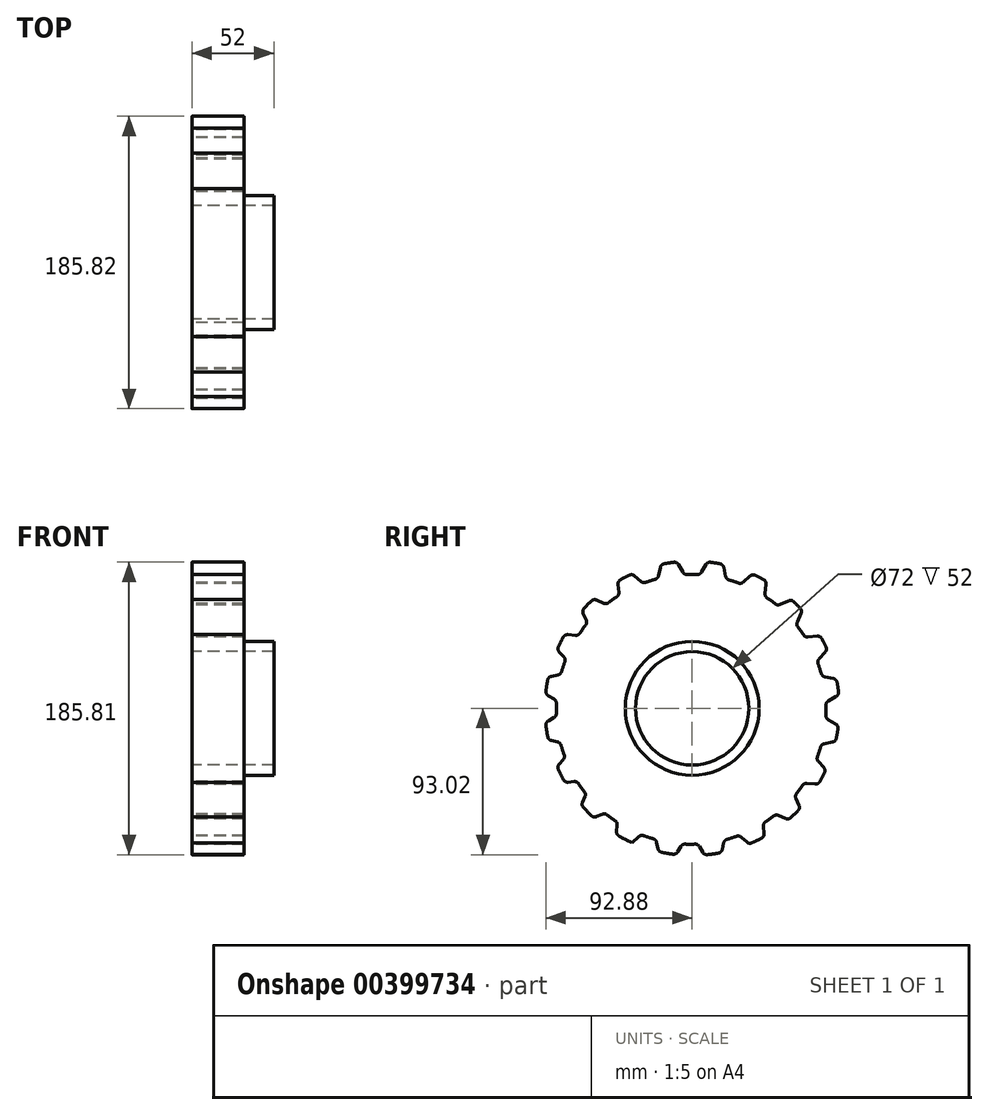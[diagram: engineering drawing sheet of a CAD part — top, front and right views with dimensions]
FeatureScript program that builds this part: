
annotation { "Feature Type Name" : "Feature", "Feature Type Description" : "" }
export const myFeature = defineFeature(function(context is Context, id is Id, definition is map)
    precondition{}
    {
        {
            var Q0;
            Q0=qCreatedBy(makeId("Right.planeOp"),FACE);
            var sketch = newSketch(context, id + "F0", { "sketchPlane" : qUnion([Q0])});
            skCircle(sketch, "E0", {"center": v(0, 0) * mm, "radius": 93.5 * mm});
            skCircle(sketch, "E1", {"center": v(0, 0) * mm, "radius": 42.5 * mm});
            skSolve(sketch);
        }
        {
            var Q0;
            Q0=makeQuery(id+"F0.imprint","IMPRINT",FACE,{"disambiguationData":[TD([[makeQuery(id+"F0.imprint","IMPRINT",EDGE,{"derivedFrom":sQuery(id+"F0.wireOp",EDGE,"E0")}),1.0]])]});
            extrude(context, id + "F1", {"entities" : qUnion([Q0]), "depth" : (347.5 + 33) * mm, "hasSecondDirection" : true, "secondDirectionOppositeDirection" : true, "secondDirectionDepth" : -347.5 * mm});
        }
        {
            var Q0;
            Q0=qCreatedBy(makeId("Right.planeOp"),FACE);
            var sketch = newSketch(context, id + "F2", { "sketchPlane" : qUnion([Q0])});
            skCircle(sketch, "E2", {"center": v(0, 0) * mm, "radius": 42.5 * mm});
            skCircle(sketch, "E3", {"center": v(0, 0) * mm, "radius": 36 * mm});
            skSolve(sketch);
        }
        {
            var Q0;
            Q0=makeQuery(id+"F2.imprint","IMPRINT",FACE,{"disambiguationData":[TD([[makeQuery(id+"F2.imprint","IMPRINT",EDGE,{"derivedFrom":sQuery(id+"F2.wireOp",EDGE,"E2")}),1.0]])]});
            extrude(context, id + "F3", {"entities" : qUnion([Q0]), "operationType" : NewBodyOperationType.ADD, "depth" : (347.5 + 52) * mm, "hasSecondDirection" : true, "secondDirectionOppositeDirection" : true, "secondDirectionDepth" : -347.5 * mm});
        }
        {
            var Q0;
            Q0=qCreatedBy(makeId("Right.planeOp"),FACE);
            var sketch = newSketch(context, id + "F4", { "sketchPlane" : qUnion([Q0])});
            skArc(sketch, "E4", {"start": v(3.2, 84.94) * mm, "mid": v(0, 85) * mm, "end": v(-3.2, 84.94) * mm});
            skCircle(sketch, "E5", {"center": v(180, 0) * mm, "radius": 95 * mm, "construction": true});
            skLineSegment(sketch, "E6", {"start": v(-5.91, 86.44) * mm, "end": v(-11.3, 95.76) * mm});
            skLineSegment(sketch, "E7", {"start": v(-11.3, 95.76) * mm, "end": v(11.3, 95.76) * mm});
            skLineSegment(sketch, "E8", {"start": v(11.3, 95.76) * mm, "end": v(5.91, 86.44) * mm});
            skLineSegment(sketch, "E9.1.0", {"start": v(-19.09, 94.74) * mm, "end": v(-21.7, 82.42) * mm});
            skArc(sketch, "E9.1.1", {"start": v(-21.7, 82.42) * mm, "mid": v(-26.5, 81.01) * mm, "end": v(-31.22, 79.33) * mm});
            skLineSegment(sketch, "E9.1.2", {"start": v(-40.58, 87.76) * mm, "end": v(-19.09, 94.74) * mm});
            skLineSegment(sketch, "E9.1.3", {"start": v(-31.22, 79.33) * mm, "end": v(-40.58, 87.76) * mm});
            skLineSegment(sketch, "E9.2.0", {"start": v(-47.67, 84.38) * mm, "end": v(-46.35, 71.85) * mm});
            skArc(sketch, "E9.2.1", {"start": v(-46.35, 71.85) * mm, "mid": v(-50.48, 69.03) * mm, "end": v(-54.44, 65.97) * mm});
            skLineSegment(sketch, "E9.2.2", {"start": v(-65.95, 71.1) * mm, "end": v(-47.67, 84.38) * mm});
            skLineSegment(sketch, "E9.2.3", {"start": v(-54.44, 65.97) * mm, "end": v(-65.95, 71.1) * mm});
            skLineSegment(sketch, "E9.3.0", {"start": v(-71.65, 65.7) * mm, "end": v(-66.52, 54.19) * mm});
            skArc(sketch, "E9.3.1", {"start": v(-66.52, 54.19) * mm, "mid": v(-69.58, 50.23) * mm, "end": v(-72.4, 46.1) * mm});
            skLineSegment(sketch, "E9.3.2", {"start": v(-84.93, 47.41) * mm, "end": v(-71.65, 65.7) * mm});
            skLineSegment(sketch, "E9.3.3", {"start": v(-72.4, 46.1) * mm, "end": v(-84.93, 47.41) * mm});
            skLineSegment(sketch, "E9.4.0", {"start": v(-88.68, 40.51) * mm, "end": v(-80.25, 31.15) * mm});
            skArc(sketch, "E9.4.1", {"start": v(-80.25, 31.15) * mm, "mid": v(-81.94, 26.44) * mm, "end": v(-83.34, 21.64) * mm});
            skLineSegment(sketch, "E9.4.2", {"start": v(-95.67, 19.02) * mm, "end": v(-88.68, 40.51) * mm});
            skLineSegment(sketch, "E9.4.3", {"start": v(-83.34, 21.64) * mm, "end": v(-95.67, 19.02) * mm});
            skLineSegment(sketch, "E9.5.0", {"start": v(-97.1, 11.3) * mm, "end": v(-86.19, 5) * mm});
            skArc(sketch, "E9.5.1", {"start": v(-86.19, 5) * mm, "mid": v(-86.34, 0) * mm, "end": v(-86.19, -5) * mm});
            skLineSegment(sketch, "E9.5.2", {"start": v(-97.1, -11.3) * mm, "end": v(-97.1, 11.3) * mm});
            skLineSegment(sketch, "E9.5.3", {"start": v(-86.19, -5) * mm, "end": v(-97.1, -11.3) * mm});
            skLineSegment(sketch, "E9.6.0", {"start": v(-96.08, -19.09) * mm, "end": v(-83.75, -21.7) * mm});
            skArc(sketch, "E9.6.1", {"start": v(-83.75, -21.7) * mm, "mid": v(-82.35, -26.5) * mm, "end": v(-80.66, -31.22) * mm});
            skLineSegment(sketch, "E9.6.2", {"start": v(-89.1, -40.58) * mm, "end": v(-96.08, -19.09) * mm});
            skLineSegment(sketch, "E9.6.3", {"start": v(-80.66, -31.22) * mm, "end": v(-89.1, -40.58) * mm});
            skLineSegment(sketch, "E9.7.0", {"start": v(-85.72, -47.67) * mm, "end": v(-73.19, -46.35) * mm});
            skArc(sketch, "E9.7.1", {"start": v(-73.19, -46.35) * mm, "mid": v(-70.37, -50.48) * mm, "end": v(-67.3, -54.44) * mm});
            skLineSegment(sketch, "E9.7.2", {"start": v(-72.43, -65.95) * mm, "end": v(-85.72, -47.67) * mm});
            skLineSegment(sketch, "E9.7.3", {"start": v(-67.3, -54.44) * mm, "end": v(-72.43, -65.95) * mm});
            skLineSegment(sketch, "E9.8.0", {"start": v(-67.03, -71.65) * mm, "end": v(-55.52, -66.52) * mm});
            skArc(sketch, "E9.8.1", {"start": v(-55.52, -66.52) * mm, "mid": v(-51.56, -69.58) * mm, "end": v(-47.43, -72.4) * mm});
            skLineSegment(sketch, "E9.8.2", {"start": v(-48.75, -84.93) * mm, "end": v(-67.03, -71.65) * mm});
            skLineSegment(sketch, "E9.8.3", {"start": v(-47.43, -72.4) * mm, "end": v(-48.75, -84.93) * mm});
            skLineSegment(sketch, "E9.9.0", {"start": v(-41.85, -88.68) * mm, "end": v(-32.49, -80.25) * mm});
            skArc(sketch, "E9.9.1", {"start": v(-32.49, -80.25) * mm, "mid": v(-27.78, -81.94) * mm, "end": v(-22.97, -83.34) * mm});
            skLineSegment(sketch, "E9.9.2", {"start": v(-20.36, -95.67) * mm, "end": v(-41.85, -88.68) * mm});
            skLineSegment(sketch, "E9.9.3", {"start": v(-22.97, -83.34) * mm, "end": v(-20.36, -95.67) * mm});
            skLineSegment(sketch, "E9.10.0", {"start": v(-12.64, -97.1) * mm, "end": v(-6.34, -86.19) * mm});
            skArc(sketch, "E9.10.1", {"start": v(-6.34, -86.19) * mm, "mid": v(-1.34, -86.34) * mm, "end": v(3.66, -86.19) * mm});
            skLineSegment(sketch, "E9.10.2", {"start": v(9.96, -97.1) * mm, "end": v(-12.64, -97.1) * mm});
            skLineSegment(sketch, "E9.10.3", {"start": v(3.66, -86.19) * mm, "end": v(9.96, -97.1) * mm});
            skLineSegment(sketch, "E9.11.0", {"start": v(17.75, -96.08) * mm, "end": v(20.37, -83.75) * mm});
            skArc(sketch, "E9.11.1", {"start": v(20.37, -83.75) * mm, "mid": v(25.17, -82.35) * mm, "end": v(29.88, -80.66) * mm});
            skLineSegment(sketch, "E9.11.2", {"start": v(39.24, -89.1) * mm, "end": v(17.75, -96.08) * mm});
            skLineSegment(sketch, "E9.11.3", {"start": v(29.88, -80.66) * mm, "end": v(39.24, -89.1) * mm});
            skLineSegment(sketch, "E9.12.0", {"start": v(46.33, -85.72) * mm, "end": v(45.01, -73.19) * mm});
            skArc(sketch, "E9.12.1", {"start": v(45.01, -73.19) * mm, "mid": v(49.15, -70.37) * mm, "end": v(53.1, -67.3) * mm});
            skLineSegment(sketch, "E9.12.2", {"start": v(64.62, -72.43) * mm, "end": v(46.33, -85.72) * mm});
            skLineSegment(sketch, "E9.12.3", {"start": v(53.1, -67.3) * mm, "end": v(64.62, -72.43) * mm});
            skLineSegment(sketch, "E9.13.0", {"start": v(70.31, -67.03) * mm, "end": v(65.19, -55.52) * mm});
            skArc(sketch, "E9.13.1", {"start": v(65.19, -55.52) * mm, "mid": v(68.25, -51.56) * mm, "end": v(71.07, -47.43) * mm});
            skLineSegment(sketch, "E9.13.2", {"start": v(83.6, -48.75) * mm, "end": v(70.31, -67.03) * mm});
            skLineSegment(sketch, "E9.13.3", {"start": v(71.07, -47.43) * mm, "end": v(83.6, -48.75) * mm});
            skLineSegment(sketch, "E9.14.0", {"start": v(87.35, -41.85) * mm, "end": v(78.92, -32.49) * mm});
            skArc(sketch, "E9.14.1", {"start": v(78.92, -32.49) * mm, "mid": v(80.6, -27.78) * mm, "end": v(82, -22.97) * mm});
            skLineSegment(sketch, "E9.14.2", {"start": v(94.33, -20.36) * mm, "end": v(87.35, -41.85) * mm});
            skLineSegment(sketch, "E9.14.3", {"start": v(82, -22.97) * mm, "end": v(94.33, -20.36) * mm});
            skLineSegment(sketch, "E9.15.0", {"start": v(95.76, -12.64) * mm, "end": v(84.85, -6.34) * mm});
            skArc(sketch, "E9.15.1", {"start": v(84.85, -6.34) * mm, "mid": v(85, -1.34) * mm, "end": v(84.85, 3.66) * mm});
            skLineSegment(sketch, "E9.15.2", {"start": v(95.76, 9.96) * mm, "end": v(95.76, -12.64) * mm});
            skLineSegment(sketch, "E9.15.3", {"start": v(84.85, 3.66) * mm, "end": v(95.76, 9.96) * mm});
            skLineSegment(sketch, "E9.16.0", {"start": v(94.74, 17.75) * mm, "end": v(82.42, 20.37) * mm});
            skArc(sketch, "E9.16.1", {"start": v(82.42, 20.37) * mm, "mid": v(81.01, 25.17) * mm, "end": v(79.33, 29.88) * mm});
            skLineSegment(sketch, "E9.16.2", {"start": v(87.76, 39.24) * mm, "end": v(94.74, 17.75) * mm});
            skLineSegment(sketch, "E9.16.3", {"start": v(79.33, 29.88) * mm, "end": v(87.76, 39.24) * mm});
            skLineSegment(sketch, "E9.17.0", {"start": v(84.38, 46.33) * mm, "end": v(71.85, 45.01) * mm});
            skArc(sketch, "E9.17.1", {"start": v(71.85, 45.01) * mm, "mid": v(69.03, 49.15) * mm, "end": v(65.97, 53.1) * mm});
            skLineSegment(sketch, "E9.17.2", {"start": v(71.1, 64.62) * mm, "end": v(84.38, 46.33) * mm});
            skLineSegment(sketch, "E9.17.3", {"start": v(65.97, 53.1) * mm, "end": v(71.1, 64.62) * mm});
            skLineSegment(sketch, "E9.18.0", {"start": v(65.7, 70.31) * mm, "end": v(54.19, 65.19) * mm});
            skArc(sketch, "E9.18.1", {"start": v(54.19, 65.19) * mm, "mid": v(50.23, 68.25) * mm, "end": v(46.1, 71.07) * mm});
            skLineSegment(sketch, "E9.18.2", {"start": v(47.41, 83.6) * mm, "end": v(65.7, 70.31) * mm});
            skLineSegment(sketch, "E9.18.3", {"start": v(46.1, 71.07) * mm, "end": v(47.41, 83.6) * mm});
            skLineSegment(sketch, "E9.19.0", {"start": v(40.51, 87.35) * mm, "end": v(31.15, 78.92) * mm});
            skArc(sketch, "E9.19.1", {"start": v(31.15, 78.92) * mm, "mid": v(26.44, 80.6) * mm, "end": v(21.64, 82) * mm});
            skLineSegment(sketch, "E9.19.2", {"start": v(19.02, 94.33) * mm, "end": v(40.51, 87.35) * mm});
            skLineSegment(sketch, "E9.19.3", {"start": v(21.64, 82) * mm, "end": v(19.02, 94.33) * mm});
            skPoint(sketch, "E9.center", {"position": v(-0.67, -0.67) * mm});
            skPoint(sketch, "E10.visualSharp", {"position": v(-5, 84.85) * mm});
            skArc(sketch, "E10.filletArc", {"start": v(-5.91, 86.44) * mm, "mid": v(-4.77, 85.31) * mm, "end": v(-3.2, 84.94) * mm});
            skPoint(sketch, "E11.visualSharp", {"position": v(5, 84.85) * mm});
            skArc(sketch, "E11.filletArc", {"start": v(3.2, 84.94) * mm, "mid": v(4.77, 85.31) * mm, "end": v(5.91, 86.44) * mm});
            skSolve(sketch);
        }
        {
            var Q0;
            Q0 = qSketchRegion(id + "F4", true);
            extrude(context, id + "F5", {"entities" : qUnion([Q0]), "depth" : 473 * mm});
        }
        {
            var Q0;
            Q0=makeQuery(id+"F5.opExtrude","SWEPT_BODY",BODY,{"disambiguationData":[OSD([sQuery(id+"F4.wireOp",EDGE,"E4"),sQuery(id+"F4.wireOp",EDGE,"E6"),sQuery(id+"F4.wireOp",EDGE,"E7"),sQuery(id+"F4.wireOp",EDGE,"E8")])]});
            var Q1;
            Q1=makeQuery(id+"F1.opExtrude","SWEPT_BODY",BODY,{"disambiguationData":[OSD([sQuery(id+"F0.wireOp",EDGE,"E0"),sQuery(id+"F0.wireOp",EDGE,"E1")])]});
            booleanBodies(context, id + "F6", {"operationType" : BooleanOperationType.SUBTRACTION, "tools" : qUnion([Q0]), "targets" : qUnion([Q1])});
        }
        {
            var Q0;
            Q0=makeQuery(id+"F5.opExtrude","SWEPT_BODY",BODY,{"disambiguationData":[OSD([sQuery(id+"F4.wireOp",EDGE,"E9.1.0"),sQuery(id+"F4.wireOp",EDGE,"E9.1.1"),sQuery(id+"F4.wireOp",EDGE,"E9.1.2"),sQuery(id+"F4.wireOp",EDGE,"E9.1.3")])]});
            var Q1;
            Q1=makeQuery(id+"F5.opExtrude","SWEPT_BODY",BODY,{"disambiguationData":[OSD([sQuery(id+"F4.wireOp",EDGE,"E9.2.0"),sQuery(id+"F4.wireOp",EDGE,"E9.2.1"),sQuery(id+"F4.wireOp",EDGE,"E9.2.2"),sQuery(id+"F4.wireOp",EDGE,"E9.2.3")])]});
            var Q2;
            Q2=makeQuery(id+"F5.opExtrude","SWEPT_BODY",BODY,{"disambiguationData":[OSD([sQuery(id+"F4.wireOp",EDGE,"E9.3.0"),sQuery(id+"F4.wireOp",EDGE,"E9.3.1"),sQuery(id+"F4.wireOp",EDGE,"E9.3.2"),sQuery(id+"F4.wireOp",EDGE,"E9.3.3")])]});
            var Q3;
            Q3=makeQuery(id+"F5.opExtrude","SWEPT_BODY",BODY,{"disambiguationData":[OSD([sQuery(id+"F4.wireOp",EDGE,"E9.4.0"),sQuery(id+"F4.wireOp",EDGE,"E9.4.1"),sQuery(id+"F4.wireOp",EDGE,"E9.4.2"),sQuery(id+"F4.wireOp",EDGE,"E9.4.3")])]});
            var Q4;
            Q4=makeQuery(id+"F5.opExtrude","SWEPT_BODY",BODY,{"disambiguationData":[OSD([sQuery(id+"F4.wireOp",EDGE,"E9.5.0"),sQuery(id+"F4.wireOp",EDGE,"E9.5.1"),sQuery(id+"F4.wireOp",EDGE,"E9.5.2"),sQuery(id+"F4.wireOp",EDGE,"E9.5.3")])]});
            var Q5;
            Q5=makeQuery(id+"F5.opExtrude","SWEPT_BODY",BODY,{"disambiguationData":[OSD([sQuery(id+"F4.wireOp",EDGE,"E9.6.0"),sQuery(id+"F4.wireOp",EDGE,"E9.6.1"),sQuery(id+"F4.wireOp",EDGE,"E9.6.2"),sQuery(id+"F4.wireOp",EDGE,"E9.6.3")])]});
            var Q6;
            Q6=makeQuery(id+"F5.opExtrude","SWEPT_BODY",BODY,{"disambiguationData":[OSD([sQuery(id+"F4.wireOp",EDGE,"E9.7.0"),sQuery(id+"F4.wireOp",EDGE,"E9.7.1"),sQuery(id+"F4.wireOp",EDGE,"E9.7.2"),sQuery(id+"F4.wireOp",EDGE,"E9.7.3")])]});
            var Q7;
            Q7=makeQuery(id+"F5.opExtrude","SWEPT_BODY",BODY,{"disambiguationData":[OSD([sQuery(id+"F4.wireOp",EDGE,"E9.8.0"),sQuery(id+"F4.wireOp",EDGE,"E9.8.1"),sQuery(id+"F4.wireOp",EDGE,"E9.8.2"),sQuery(id+"F4.wireOp",EDGE,"E9.8.3")])]});
            var Q8;
            Q8=makeQuery(id+"F5.opExtrude","SWEPT_BODY",BODY,{"disambiguationData":[OSD([sQuery(id+"F4.wireOp",EDGE,"E9.9.0"),sQuery(id+"F4.wireOp",EDGE,"E9.9.1"),sQuery(id+"F4.wireOp",EDGE,"E9.9.2"),sQuery(id+"F4.wireOp",EDGE,"E9.9.3")])]});
            var Q9;
            Q9=makeQuery(id+"F5.opExtrude","SWEPT_BODY",BODY,{"disambiguationData":[OSD([sQuery(id+"F4.wireOp",EDGE,"E9.10.0"),sQuery(id+"F4.wireOp",EDGE,"E9.10.1"),sQuery(id+"F4.wireOp",EDGE,"E9.10.2"),sQuery(id+"F4.wireOp",EDGE,"E9.10.3")])]});
            var Q10;
            Q10=makeQuery(id+"F5.opExtrude","SWEPT_BODY",BODY,{"disambiguationData":[OSD([sQuery(id+"F4.wireOp",EDGE,"E9.11.0"),sQuery(id+"F4.wireOp",EDGE,"E9.11.1"),sQuery(id+"F4.wireOp",EDGE,"E9.11.2"),sQuery(id+"F4.wireOp",EDGE,"E9.11.3")])]});
            var Q11;
            Q11=makeQuery(id+"F5.opExtrude","SWEPT_BODY",BODY,{"disambiguationData":[OSD([sQuery(id+"F4.wireOp",EDGE,"E9.12.0"),sQuery(id+"F4.wireOp",EDGE,"E9.12.1"),sQuery(id+"F4.wireOp",EDGE,"E9.12.2"),sQuery(id+"F4.wireOp",EDGE,"E9.12.3")])]});
            var Q12;
            Q12=makeQuery(id+"F5.opExtrude","SWEPT_BODY",BODY,{"disambiguationData":[OSD([sQuery(id+"F4.wireOp",EDGE,"E9.13.0"),sQuery(id+"F4.wireOp",EDGE,"E9.13.1"),sQuery(id+"F4.wireOp",EDGE,"E9.13.2"),sQuery(id+"F4.wireOp",EDGE,"E9.13.3")])]});
            var Q13;
            Q13=makeQuery(id+"F5.opExtrude","SWEPT_BODY",BODY,{"disambiguationData":[OSD([sQuery(id+"F4.wireOp",EDGE,"E9.14.0"),sQuery(id+"F4.wireOp",EDGE,"E9.14.1"),sQuery(id+"F4.wireOp",EDGE,"E9.14.2"),sQuery(id+"F4.wireOp",EDGE,"E9.14.3")])]});
            var Q14;
            Q14=makeQuery(id+"F5.opExtrude","SWEPT_BODY",BODY,{"disambiguationData":[OSD([sQuery(id+"F4.wireOp",EDGE,"E9.15.0"),sQuery(id+"F4.wireOp",EDGE,"E9.15.1"),sQuery(id+"F4.wireOp",EDGE,"E9.15.2"),sQuery(id+"F4.wireOp",EDGE,"E9.15.3")])]});
            var Q15;
            Q15=makeQuery(id+"F5.opExtrude","SWEPT_BODY",BODY,{"disambiguationData":[OSD([sQuery(id+"F4.wireOp",EDGE,"E9.16.0"),sQuery(id+"F4.wireOp",EDGE,"E9.16.1"),sQuery(id+"F4.wireOp",EDGE,"E9.16.2"),sQuery(id+"F4.wireOp",EDGE,"E9.16.3")])]});
            var Q16;
            Q16=makeQuery(id+"F5.opExtrude","SWEPT_BODY",BODY,{"disambiguationData":[OSD([sQuery(id+"F4.wireOp",EDGE,"E9.17.0"),sQuery(id+"F4.wireOp",EDGE,"E9.17.1"),sQuery(id+"F4.wireOp",EDGE,"E9.17.2"),sQuery(id+"F4.wireOp",EDGE,"E9.17.3")])]});
            var Q17;
            Q17=makeQuery(id+"F5.opExtrude","SWEPT_BODY",BODY,{"disambiguationData":[OSD([sQuery(id+"F4.wireOp",EDGE,"E9.18.0"),sQuery(id+"F4.wireOp",EDGE,"E9.18.1"),sQuery(id+"F4.wireOp",EDGE,"E9.18.2"),sQuery(id+"F4.wireOp",EDGE,"E9.18.3")])]});
            var Q18;
            Q18=makeQuery(id+"F5.opExtrude","SWEPT_BODY",BODY,{"disambiguationData":[OSD([sQuery(id+"F4.wireOp",EDGE,"E9.19.0"),sQuery(id+"F4.wireOp",EDGE,"E9.19.1"),sQuery(id+"F4.wireOp",EDGE,"E9.19.2"),sQuery(id+"F4.wireOp",EDGE,"E9.19.3")])]});
            var Q19;
            Q19=makeQuery(id+"F1.opExtrude","SWEPT_BODY",BODY,{"disambiguationData":[OSD([sQuery(id+"F0.wireOp",EDGE,"E0"),sQuery(id+"F0.wireOp",EDGE,"E1")])]});
            booleanBodies(context, id + "F7", {"operationType" : BooleanOperationType.SUBTRACTION, "tools" : qUnion([Q0, Q1, Q2, Q3, Q4, Q5, Q6, Q7, Q8, Q9, Q10, Q11, Q12, Q13, Q14, Q15, Q16, Q17, Q18]), "targets" : qUnion([Q19])});
        }
        {
            var Q0;
            Q0=makeQuery(id+"F6.opBoolean","INTERSECT",EDGE,{"derivedFrom":[makeQuery(id+"F1.opExtrude","SWEPT_FACE",FACE,{"disambiguationData":[OSD([sQuery(id+"F0.wireOp",EDGE,"E0")])]}),makeQuery(id+"F5.opExtrude","SWEPT_FACE",FACE,{"disambiguationData":[OSD([sQuery(id+"F4.wireOp",EDGE,"E6")])]})]});
            var Q1;
            Q1=makeQuery(id+"F7.opBoolean","INTERSECT",EDGE,{"derivedFrom":[makeQuery(id+"F5.opExtrude","SWEPT_FACE",FACE,{"disambiguationData":[OSD([sQuery(id+"F4.wireOp",EDGE,"E9.1.0")])]}),makeQuery(id+"F1.opExtrude","SWEPT_FACE",FACE,{"disambiguationData":[OSD([sQuery(id+"F0.wireOp",EDGE,"E0")])]})]});
            var Q2;
            Q2=makeQuery(id+"F7.opBoolean","COPY",EDGE,{"derivedFrom":makeQuery(id+"F5.opExtrude","SWEPT_EDGE",EDGE,{"disambiguationData":[OSD([sQuery(id+"F4.wireOp",EDGE,"E9.1.0"),sQuery(id+"F4.wireOp",EDGE,"E9.1.1")])]})});
            var Q3;
            Q3=makeQuery(id+"F7.opBoolean","INTERSECT",EDGE,{"derivedFrom":[makeQuery(id+"F5.opExtrude","SWEPT_FACE",FACE,{"disambiguationData":[OSD([sQuery(id+"F4.wireOp",EDGE,"E9.1.3")])]}),makeQuery(id+"F1.opExtrude","SWEPT_FACE",FACE,{"disambiguationData":[OSD([sQuery(id+"F0.wireOp",EDGE,"E0")])]})]});
            var Q4;
            Q4=makeQuery(id+"F7.opBoolean","INTERSECT",EDGE,{"derivedFrom":[makeQuery(id+"F5.opExtrude","SWEPT_FACE",FACE,{"disambiguationData":[OSD([sQuery(id+"F4.wireOp",EDGE,"E9.2.0")])]}),makeQuery(id+"F1.opExtrude","SWEPT_FACE",FACE,{"disambiguationData":[OSD([sQuery(id+"F0.wireOp",EDGE,"E0")])]})]});
            var Q5;
            Q5=makeQuery(id+"F7.opBoolean","COPY",EDGE,{"derivedFrom":makeQuery(id+"F5.opExtrude","SWEPT_EDGE",EDGE,{"disambiguationData":[OSD([sQuery(id+"F4.wireOp",EDGE,"E9.2.0"),sQuery(id+"F4.wireOp",EDGE,"E9.2.1")])]})});
            var Q6;
            Q6=makeQuery(id+"F7.opBoolean","COPY",EDGE,{"derivedFrom":makeQuery(id+"F5.opExtrude","SWEPT_EDGE",EDGE,{"disambiguationData":[OSD([sQuery(id+"F4.wireOp",EDGE,"E9.2.1"),sQuery(id+"F4.wireOp",EDGE,"E9.2.3")])]})});
            var Q7;
            Q7=makeQuery(id+"F7.opBoolean","INTERSECT",EDGE,{"derivedFrom":[makeQuery(id+"F5.opExtrude","SWEPT_FACE",FACE,{"disambiguationData":[OSD([sQuery(id+"F4.wireOp",EDGE,"E9.2.3")])]}),makeQuery(id+"F1.opExtrude","SWEPT_FACE",FACE,{"disambiguationData":[OSD([sQuery(id+"F0.wireOp",EDGE,"E0")])]})]});
            var Q8;
            Q8=makeQuery(id+"F7.opBoolean","INTERSECT",EDGE,{"derivedFrom":[makeQuery(id+"F5.opExtrude","SWEPT_FACE",FACE,{"disambiguationData":[OSD([sQuery(id+"F4.wireOp",EDGE,"E9.3.0")])]}),makeQuery(id+"F1.opExtrude","SWEPT_FACE",FACE,{"disambiguationData":[OSD([sQuery(id+"F0.wireOp",EDGE,"E0")])]})]});
            var Q9;
            Q9=makeQuery(id+"F7.opBoolean","COPY",EDGE,{"derivedFrom":makeQuery(id+"F5.opExtrude","SWEPT_EDGE",EDGE,{"disambiguationData":[OSD([sQuery(id+"F4.wireOp",EDGE,"E9.3.0"),sQuery(id+"F4.wireOp",EDGE,"E9.3.1")])]})});
            var Q10;
            Q10=makeQuery(id+"F7.opBoolean","COPY",EDGE,{"derivedFrom":makeQuery(id+"F5.opExtrude","SWEPT_EDGE",EDGE,{"disambiguationData":[OSD([sQuery(id+"F4.wireOp",EDGE,"E9.3.1"),sQuery(id+"F4.wireOp",EDGE,"E9.3.3")])]})});
            var Q11;
            Q11=makeQuery(id+"F7.opBoolean","INTERSECT",EDGE,{"derivedFrom":[makeQuery(id+"F5.opExtrude","SWEPT_FACE",FACE,{"disambiguationData":[OSD([sQuery(id+"F4.wireOp",EDGE,"E9.3.3")])]}),makeQuery(id+"F1.opExtrude","SWEPT_FACE",FACE,{"disambiguationData":[OSD([sQuery(id+"F0.wireOp",EDGE,"E0")])]})]});
            var Q12;
            Q12=makeQuery(id+"F7.opBoolean","INTERSECT",EDGE,{"derivedFrom":[makeQuery(id+"F5.opExtrude","SWEPT_FACE",FACE,{"disambiguationData":[OSD([sQuery(id+"F4.wireOp",EDGE,"E9.4.0")])]}),makeQuery(id+"F1.opExtrude","SWEPT_FACE",FACE,{"disambiguationData":[OSD([sQuery(id+"F0.wireOp",EDGE,"E0")])]})]});
            var Q13;
            Q13=makeQuery(id+"F7.opBoolean","INTERSECT",EDGE,{"derivedFrom":[makeQuery(id+"F5.opExtrude","SWEPT_FACE",FACE,{"disambiguationData":[OSD([sQuery(id+"F4.wireOp",EDGE,"E9.4.3")])]}),makeQuery(id+"F1.opExtrude","SWEPT_FACE",FACE,{"disambiguationData":[OSD([sQuery(id+"F0.wireOp",EDGE,"E0")])]})]});
            var Q14;
            Q14=makeQuery(id+"F7.opBoolean","INTERSECT",EDGE,{"derivedFrom":[makeQuery(id+"F5.opExtrude","SWEPT_FACE",FACE,{"disambiguationData":[OSD([sQuery(id+"F4.wireOp",EDGE,"E9.5.0")])]}),makeQuery(id+"F1.opExtrude","SWEPT_FACE",FACE,{"disambiguationData":[OSD([sQuery(id+"F0.wireOp",EDGE,"E0")])]})]});
            var Q15;
            Q15=makeQuery(id+"F7.opBoolean","INTERSECT",EDGE,{"derivedFrom":[makeQuery(id+"F5.opExtrude","SWEPT_FACE",FACE,{"disambiguationData":[OSD([sQuery(id+"F4.wireOp",EDGE,"E9.5.3")])]}),makeQuery(id+"F1.opExtrude","SWEPT_FACE",FACE,{"disambiguationData":[OSD([sQuery(id+"F0.wireOp",EDGE,"E0")])]})]});
            var Q16;
            Q16=makeQuery(id+"F7.opBoolean","COPY",EDGE,{"derivedFrom":makeQuery(id+"F5.opExtrude","SWEPT_EDGE",EDGE,{"disambiguationData":[OSD([sQuery(id+"F4.wireOp",EDGE,"E9.4.0"),sQuery(id+"F4.wireOp",EDGE,"E9.4.1")])]})});
            var Q17;
            Q17=makeQuery(id+"F7.opBoolean","COPY",EDGE,{"derivedFrom":makeQuery(id+"F5.opExtrude","SWEPT_EDGE",EDGE,{"disambiguationData":[OSD([sQuery(id+"F4.wireOp",EDGE,"E9.4.1"),sQuery(id+"F4.wireOp",EDGE,"E9.4.3")])]})});
            var Q18;
            Q18=makeQuery(id+"F7.opBoolean","COPY",EDGE,{"derivedFrom":makeQuery(id+"F5.opExtrude","SWEPT_EDGE",EDGE,{"disambiguationData":[OSD([sQuery(id+"F4.wireOp",EDGE,"E9.5.0"),sQuery(id+"F4.wireOp",EDGE,"E9.5.1")])]})});
            var Q19;
            Q19=makeQuery(id+"F7.opBoolean","COPY",EDGE,{"derivedFrom":makeQuery(id+"F5.opExtrude","SWEPT_EDGE",EDGE,{"disambiguationData":[OSD([sQuery(id+"F4.wireOp",EDGE,"E9.5.1"),sQuery(id+"F4.wireOp",EDGE,"E9.5.3")])]})});
            var Q20;
            Q20=makeQuery(id+"F7.opBoolean","INTERSECT",EDGE,{"derivedFrom":[makeQuery(id+"F5.opExtrude","SWEPT_FACE",FACE,{"disambiguationData":[OSD([sQuery(id+"F4.wireOp",EDGE,"E9.6.0")])]}),makeQuery(id+"F1.opExtrude","SWEPT_FACE",FACE,{"disambiguationData":[OSD([sQuery(id+"F0.wireOp",EDGE,"E0")])]})]});
            var Q21;
            Q21=makeQuery(id+"F7.opBoolean","COPY",EDGE,{"derivedFrom":makeQuery(id+"F5.opExtrude","SWEPT_EDGE",EDGE,{"disambiguationData":[OSD([sQuery(id+"F4.wireOp",EDGE,"E9.6.0"),sQuery(id+"F4.wireOp",EDGE,"E9.6.1")])]})});
            var Q22;
            Q22=makeQuery(id+"F7.opBoolean","COPY",EDGE,{"derivedFrom":makeQuery(id+"F5.opExtrude","SWEPT_EDGE",EDGE,{"disambiguationData":[OSD([sQuery(id+"F4.wireOp",EDGE,"E9.6.1"),sQuery(id+"F4.wireOp",EDGE,"E9.6.3")])]})});
            var Q23;
            Q23=makeQuery(id+"F7.opBoolean","INTERSECT",EDGE,{"derivedFrom":[makeQuery(id+"F5.opExtrude","SWEPT_FACE",FACE,{"disambiguationData":[OSD([sQuery(id+"F4.wireOp",EDGE,"E9.6.3")])]}),makeQuery(id+"F1.opExtrude","SWEPT_FACE",FACE,{"disambiguationData":[OSD([sQuery(id+"F0.wireOp",EDGE,"E0")])]})]});
            var Q24;
            Q24=makeQuery(id+"F7.opBoolean","INTERSECT",EDGE,{"derivedFrom":[makeQuery(id+"F5.opExtrude","SWEPT_FACE",FACE,{"disambiguationData":[OSD([sQuery(id+"F4.wireOp",EDGE,"E9.7.0")])]}),makeQuery(id+"F1.opExtrude","SWEPT_FACE",FACE,{"disambiguationData":[OSD([sQuery(id+"F0.wireOp",EDGE,"E0")])]})]});
            var Q25;
            Q25=makeQuery(id+"F7.opBoolean","COPY",EDGE,{"derivedFrom":makeQuery(id+"F5.opExtrude","SWEPT_EDGE",EDGE,{"disambiguationData":[OSD([sQuery(id+"F4.wireOp",EDGE,"E9.7.0"),sQuery(id+"F4.wireOp",EDGE,"E9.7.1")])]})});
            var Q26;
            Q26=makeQuery(id+"F7.opBoolean","COPY",EDGE,{"derivedFrom":makeQuery(id+"F5.opExtrude","SWEPT_EDGE",EDGE,{"disambiguationData":[OSD([sQuery(id+"F4.wireOp",EDGE,"E9.7.1"),sQuery(id+"F4.wireOp",EDGE,"E9.7.3")])]})});
            var Q27;
            Q27=makeQuery(id+"F7.opBoolean","INTERSECT",EDGE,{"derivedFrom":[makeQuery(id+"F5.opExtrude","SWEPT_FACE",FACE,{"disambiguationData":[OSD([sQuery(id+"F4.wireOp",EDGE,"E9.7.3")])]}),makeQuery(id+"F1.opExtrude","SWEPT_FACE",FACE,{"disambiguationData":[OSD([sQuery(id+"F0.wireOp",EDGE,"E0")])]})]});
            var Q28;
            Q28=makeQuery(id+"F7.opBoolean","INTERSECT",EDGE,{"derivedFrom":[makeQuery(id+"F5.opExtrude","SWEPT_FACE",FACE,{"disambiguationData":[OSD([sQuery(id+"F4.wireOp",EDGE,"E9.8.0")])]}),makeQuery(id+"F1.opExtrude","SWEPT_FACE",FACE,{"disambiguationData":[OSD([sQuery(id+"F0.wireOp",EDGE,"E0")])]})]});
            var Q29;
            Q29=makeQuery(id+"F7.opBoolean","COPY",EDGE,{"derivedFrom":makeQuery(id+"F5.opExtrude","SWEPT_EDGE",EDGE,{"disambiguationData":[OSD([sQuery(id+"F4.wireOp",EDGE,"E9.8.0"),sQuery(id+"F4.wireOp",EDGE,"E9.8.1")])]})});
            var Q30;
            Q30=makeQuery(id+"F7.opBoolean","COPY",EDGE,{"derivedFrom":makeQuery(id+"F5.opExtrude","SWEPT_EDGE",EDGE,{"disambiguationData":[OSD([sQuery(id+"F4.wireOp",EDGE,"E9.8.1"),sQuery(id+"F4.wireOp",EDGE,"E9.8.3")])]})});
            var Q31;
            Q31=makeQuery(id+"F7.opBoolean","INTERSECT",EDGE,{"derivedFrom":[makeQuery(id+"F5.opExtrude","SWEPT_FACE",FACE,{"disambiguationData":[OSD([sQuery(id+"F4.wireOp",EDGE,"E9.8.3")])]}),makeQuery(id+"F1.opExtrude","SWEPT_FACE",FACE,{"disambiguationData":[OSD([sQuery(id+"F0.wireOp",EDGE,"E0")])]})]});
            var Q32;
            Q32=makeQuery(id+"F7.opBoolean","COPY",EDGE,{"derivedFrom":makeQuery(id+"F5.opExtrude","SWEPT_EDGE",EDGE,{"disambiguationData":[OSD([sQuery(id+"F4.wireOp",EDGE,"E9.9.0"),sQuery(id+"F4.wireOp",EDGE,"E9.9.1")])]})});
            var Q33;
            Q33=makeQuery(id+"F7.opBoolean","COPY",EDGE,{"derivedFrom":makeQuery(id+"F5.opExtrude","SWEPT_EDGE",EDGE,{"disambiguationData":[OSD([sQuery(id+"F4.wireOp",EDGE,"E9.9.1"),sQuery(id+"F4.wireOp",EDGE,"E9.9.3")])]})});
            var Q34;
            Q34=makeQuery(id+"F7.opBoolean","INTERSECT",EDGE,{"derivedFrom":[makeQuery(id+"F5.opExtrude","SWEPT_FACE",FACE,{"disambiguationData":[OSD([sQuery(id+"F4.wireOp",EDGE,"E9.9.3")])]}),makeQuery(id+"F1.opExtrude","SWEPT_FACE",FACE,{"disambiguationData":[OSD([sQuery(id+"F0.wireOp",EDGE,"E0")])]})]});
            var Q35;
            Q35=makeQuery(id+"F7.opBoolean","INTERSECT",EDGE,{"derivedFrom":[makeQuery(id+"F5.opExtrude","SWEPT_FACE",FACE,{"disambiguationData":[OSD([sQuery(id+"F4.wireOp",EDGE,"E9.10.0")])]}),makeQuery(id+"F1.opExtrude","SWEPT_FACE",FACE,{"disambiguationData":[OSD([sQuery(id+"F0.wireOp",EDGE,"E0")])]})]});
            var Q36;
            Q36=makeQuery(id+"F7.opBoolean","COPY",EDGE,{"derivedFrom":makeQuery(id+"F5.opExtrude","SWEPT_EDGE",EDGE,{"disambiguationData":[OSD([sQuery(id+"F4.wireOp",EDGE,"E9.10.0"),sQuery(id+"F4.wireOp",EDGE,"E9.10.1")])]})});
            var Q37;
            Q37=makeQuery(id+"F7.opBoolean","COPY",EDGE,{"derivedFrom":makeQuery(id+"F5.opExtrude","SWEPT_EDGE",EDGE,{"disambiguationData":[OSD([sQuery(id+"F4.wireOp",EDGE,"E9.10.1"),sQuery(id+"F4.wireOp",EDGE,"E9.10.3")])]})});
            var Q38;
            Q38=makeQuery(id+"F7.opBoolean","INTERSECT",EDGE,{"derivedFrom":[makeQuery(id+"F5.opExtrude","SWEPT_FACE",FACE,{"disambiguationData":[OSD([sQuery(id+"F4.wireOp",EDGE,"E9.10.3")])]}),makeQuery(id+"F1.opExtrude","SWEPT_FACE",FACE,{"disambiguationData":[OSD([sQuery(id+"F0.wireOp",EDGE,"E0")])]})]});
            var Q39;
            Q39=makeQuery(id+"F7.opBoolean","INTERSECT",EDGE,{"derivedFrom":[makeQuery(id+"F5.opExtrude","SWEPT_FACE",FACE,{"disambiguationData":[OSD([sQuery(id+"F4.wireOp",EDGE,"E9.11.0")])]}),makeQuery(id+"F1.opExtrude","SWEPT_FACE",FACE,{"disambiguationData":[OSD([sQuery(id+"F0.wireOp",EDGE,"E0")])]})]});
            var Q40;
            Q40=makeQuery(id+"F7.opBoolean","COPY",EDGE,{"derivedFrom":makeQuery(id+"F5.opExtrude","SWEPT_EDGE",EDGE,{"disambiguationData":[OSD([sQuery(id+"F4.wireOp",EDGE,"E9.11.0"),sQuery(id+"F4.wireOp",EDGE,"E9.11.1")])]})});
            var Q41;
            Q41=makeQuery(id+"F7.opBoolean","COPY",EDGE,{"derivedFrom":makeQuery(id+"F5.opExtrude","SWEPT_EDGE",EDGE,{"disambiguationData":[OSD([sQuery(id+"F4.wireOp",EDGE,"E9.11.1"),sQuery(id+"F4.wireOp",EDGE,"E9.11.3")])]})});
            var Q42;
            Q42=makeQuery(id+"F7.opBoolean","INTERSECT",EDGE,{"derivedFrom":[makeQuery(id+"F5.opExtrude","SWEPT_FACE",FACE,{"disambiguationData":[OSD([sQuery(id+"F4.wireOp",EDGE,"E9.11.3")])]}),makeQuery(id+"F1.opExtrude","SWEPT_FACE",FACE,{"disambiguationData":[OSD([sQuery(id+"F0.wireOp",EDGE,"E0")])]})]});
            var Q43;
            Q43=makeQuery(id+"F7.opBoolean","INTERSECT",EDGE,{"derivedFrom":[makeQuery(id+"F5.opExtrude","SWEPT_FACE",FACE,{"disambiguationData":[OSD([sQuery(id+"F4.wireOp",EDGE,"E9.12.0")])]}),makeQuery(id+"F1.opExtrude","SWEPT_FACE",FACE,{"disambiguationData":[OSD([sQuery(id+"F0.wireOp",EDGE,"E0")])]})]});
            var Q44;
            Q44=makeQuery(id+"F7.opBoolean","COPY",EDGE,{"derivedFrom":makeQuery(id+"F5.opExtrude","SWEPT_EDGE",EDGE,{"disambiguationData":[OSD([sQuery(id+"F4.wireOp",EDGE,"E9.12.0"),sQuery(id+"F4.wireOp",EDGE,"E9.12.1")])]})});
            var Q45;
            Q45=makeQuery(id+"F7.opBoolean","COPY",EDGE,{"derivedFrom":makeQuery(id+"F5.opExtrude","SWEPT_EDGE",EDGE,{"disambiguationData":[OSD([sQuery(id+"F4.wireOp",EDGE,"E9.12.1"),sQuery(id+"F4.wireOp",EDGE,"E9.12.3")])]})});
            var Q46;
            Q46=makeQuery(id+"F7.opBoolean","INTERSECT",EDGE,{"derivedFrom":[makeQuery(id+"F5.opExtrude","SWEPT_FACE",FACE,{"disambiguationData":[OSD([sQuery(id+"F4.wireOp",EDGE,"E9.12.3")])]}),makeQuery(id+"F1.opExtrude","SWEPT_FACE",FACE,{"disambiguationData":[OSD([sQuery(id+"F0.wireOp",EDGE,"E0")])]})]});
            var Q47;
            Q47=makeQuery(id+"F7.opBoolean","INTERSECT",EDGE,{"derivedFrom":[makeQuery(id+"F5.opExtrude","SWEPT_FACE",FACE,{"disambiguationData":[OSD([sQuery(id+"F4.wireOp",EDGE,"E9.13.0")])]}),makeQuery(id+"F1.opExtrude","SWEPT_FACE",FACE,{"disambiguationData":[OSD([sQuery(id+"F0.wireOp",EDGE,"E0")])]})]});
            var Q48;
            Q48=makeQuery(id+"F7.opBoolean","COPY",EDGE,{"derivedFrom":makeQuery(id+"F5.opExtrude","SWEPT_EDGE",EDGE,{"disambiguationData":[OSD([sQuery(id+"F4.wireOp",EDGE,"E9.13.0"),sQuery(id+"F4.wireOp",EDGE,"E9.13.1")])]})});
            var Q49;
            Q49=makeQuery(id+"F7.opBoolean","COPY",EDGE,{"derivedFrom":makeQuery(id+"F5.opExtrude","SWEPT_EDGE",EDGE,{"disambiguationData":[OSD([sQuery(id+"F4.wireOp",EDGE,"E9.13.1"),sQuery(id+"F4.wireOp",EDGE,"E9.13.3")])]})});
            var Q50;
            Q50=makeQuery(id+"F7.opBoolean","INTERSECT",EDGE,{"derivedFrom":[makeQuery(id+"F5.opExtrude","SWEPT_FACE",FACE,{"disambiguationData":[OSD([sQuery(id+"F4.wireOp",EDGE,"E9.13.3")])]}),makeQuery(id+"F1.opExtrude","SWEPT_FACE",FACE,{"disambiguationData":[OSD([sQuery(id+"F0.wireOp",EDGE,"E0")])]})]});
            var Q51;
            Q51=makeQuery(id+"F7.opBoolean","INTERSECT",EDGE,{"derivedFrom":[makeQuery(id+"F5.opExtrude","SWEPT_FACE",FACE,{"disambiguationData":[OSD([sQuery(id+"F4.wireOp",EDGE,"E9.14.0")])]}),makeQuery(id+"F1.opExtrude","SWEPT_FACE",FACE,{"disambiguationData":[OSD([sQuery(id+"F0.wireOp",EDGE,"E0")])]})]});
            var Q52;
            Q52=makeQuery(id+"F7.opBoolean","COPY",EDGE,{"derivedFrom":makeQuery(id+"F5.opExtrude","SWEPT_EDGE",EDGE,{"disambiguationData":[OSD([sQuery(id+"F4.wireOp",EDGE,"E9.14.0"),sQuery(id+"F4.wireOp",EDGE,"E9.14.1")])]})});
            var Q53;
            Q53=makeQuery(id+"F7.opBoolean","COPY",EDGE,{"derivedFrom":makeQuery(id+"F5.opExtrude","SWEPT_EDGE",EDGE,{"disambiguationData":[OSD([sQuery(id+"F4.wireOp",EDGE,"E9.14.1"),sQuery(id+"F4.wireOp",EDGE,"E9.14.3")])]})});
            var Q54;
            Q54=makeQuery(id+"F7.opBoolean","INTERSECT",EDGE,{"derivedFrom":[makeQuery(id+"F5.opExtrude","SWEPT_FACE",FACE,{"disambiguationData":[OSD([sQuery(id+"F4.wireOp",EDGE,"E9.14.3")])]}),makeQuery(id+"F1.opExtrude","SWEPT_FACE",FACE,{"disambiguationData":[OSD([sQuery(id+"F0.wireOp",EDGE,"E0")])]})]});
            var Q55;
            Q55=makeQuery(id+"F7.opBoolean","INTERSECT",EDGE,{"derivedFrom":[makeQuery(id+"F5.opExtrude","SWEPT_FACE",FACE,{"disambiguationData":[OSD([sQuery(id+"F4.wireOp",EDGE,"E9.15.0")])]}),makeQuery(id+"F1.opExtrude","SWEPT_FACE",FACE,{"disambiguationData":[OSD([sQuery(id+"F0.wireOp",EDGE,"E0")])]})]});
            var Q56;
            Q56=makeQuery(id+"F7.opBoolean","COPY",EDGE,{"derivedFrom":makeQuery(id+"F5.opExtrude","SWEPT_EDGE",EDGE,{"disambiguationData":[OSD([sQuery(id+"F4.wireOp",EDGE,"E9.15.0"),sQuery(id+"F4.wireOp",EDGE,"E9.15.1")])]})});
            var Q57;
            Q57=makeQuery(id+"F7.opBoolean","COPY",EDGE,{"derivedFrom":makeQuery(id+"F5.opExtrude","SWEPT_EDGE",EDGE,{"disambiguationData":[OSD([sQuery(id+"F4.wireOp",EDGE,"E9.15.1"),sQuery(id+"F4.wireOp",EDGE,"E9.15.3")])]})});
            var Q58;
            Q58=makeQuery(id+"F7.opBoolean","INTERSECT",EDGE,{"derivedFrom":[makeQuery(id+"F5.opExtrude","SWEPT_FACE",FACE,{"disambiguationData":[OSD([sQuery(id+"F4.wireOp",EDGE,"E9.15.3")])]}),makeQuery(id+"F1.opExtrude","SWEPT_FACE",FACE,{"disambiguationData":[OSD([sQuery(id+"F0.wireOp",EDGE,"E0")])]})]});
            var Q59;
            Q59=makeQuery(id+"F7.opBoolean","INTERSECT",EDGE,{"derivedFrom":[makeQuery(id+"F5.opExtrude","SWEPT_FACE",FACE,{"disambiguationData":[OSD([sQuery(id+"F4.wireOp",EDGE,"E9.16.0")])]}),makeQuery(id+"F1.opExtrude","SWEPT_FACE",FACE,{"disambiguationData":[OSD([sQuery(id+"F0.wireOp",EDGE,"E0")])]})]});
            var Q60;
            Q60=makeQuery(id+"F7.opBoolean","COPY",EDGE,{"derivedFrom":makeQuery(id+"F5.opExtrude","SWEPT_EDGE",EDGE,{"disambiguationData":[OSD([sQuery(id+"F4.wireOp",EDGE,"E9.16.0"),sQuery(id+"F4.wireOp",EDGE,"E9.16.1")])]})});
            var Q61;
            Q61=makeQuery(id+"F7.opBoolean","COPY",EDGE,{"derivedFrom":makeQuery(id+"F5.opExtrude","SWEPT_EDGE",EDGE,{"disambiguationData":[OSD([sQuery(id+"F4.wireOp",EDGE,"E9.16.1"),sQuery(id+"F4.wireOp",EDGE,"E9.16.3")])]})});
            var Q62;
            Q62=makeQuery(id+"F7.opBoolean","INTERSECT",EDGE,{"derivedFrom":[makeQuery(id+"F5.opExtrude","SWEPT_FACE",FACE,{"disambiguationData":[OSD([sQuery(id+"F4.wireOp",EDGE,"E9.16.3")])]}),makeQuery(id+"F1.opExtrude","SWEPT_FACE",FACE,{"disambiguationData":[OSD([sQuery(id+"F0.wireOp",EDGE,"E0")])]})]});
            var Q63;
            Q63=makeQuery(id+"F7.opBoolean","INTERSECT",EDGE,{"derivedFrom":[makeQuery(id+"F5.opExtrude","SWEPT_FACE",FACE,{"disambiguationData":[OSD([sQuery(id+"F4.wireOp",EDGE,"E9.17.0")])]}),makeQuery(id+"F1.opExtrude","SWEPT_FACE",FACE,{"disambiguationData":[OSD([sQuery(id+"F0.wireOp",EDGE,"E0")])]})]});
            var Q64;
            Q64=makeQuery(id+"F7.opBoolean","COPY",EDGE,{"derivedFrom":makeQuery(id+"F5.opExtrude","SWEPT_EDGE",EDGE,{"disambiguationData":[OSD([sQuery(id+"F4.wireOp",EDGE,"E9.17.0"),sQuery(id+"F4.wireOp",EDGE,"E9.17.1")])]})});
            var Q65;
            Q65=makeQuery(id+"F7.opBoolean","COPY",EDGE,{"derivedFrom":makeQuery(id+"F5.opExtrude","SWEPT_EDGE",EDGE,{"disambiguationData":[OSD([sQuery(id+"F4.wireOp",EDGE,"E9.17.1"),sQuery(id+"F4.wireOp",EDGE,"E9.17.3")])]})});
            var Q66;
            Q66=makeQuery(id+"F7.opBoolean","INTERSECT",EDGE,{"derivedFrom":[makeQuery(id+"F5.opExtrude","SWEPT_FACE",FACE,{"disambiguationData":[OSD([sQuery(id+"F4.wireOp",EDGE,"E9.17.3")])]}),makeQuery(id+"F1.opExtrude","SWEPT_FACE",FACE,{"disambiguationData":[OSD([sQuery(id+"F0.wireOp",EDGE,"E0")])]})]});
            var Q67;
            Q67=makeQuery(id+"F7.opBoolean","INTERSECT",EDGE,{"derivedFrom":[makeQuery(id+"F5.opExtrude","SWEPT_FACE",FACE,{"disambiguationData":[OSD([sQuery(id+"F4.wireOp",EDGE,"E9.18.0")])]}),makeQuery(id+"F1.opExtrude","SWEPT_FACE",FACE,{"disambiguationData":[OSD([sQuery(id+"F0.wireOp",EDGE,"E0")])]})]});
            var Q68;
            Q68=makeQuery(id+"F7.opBoolean","COPY",EDGE,{"derivedFrom":makeQuery(id+"F5.opExtrude","SWEPT_EDGE",EDGE,{"disambiguationData":[OSD([sQuery(id+"F4.wireOp",EDGE,"E9.18.0"),sQuery(id+"F4.wireOp",EDGE,"E9.18.1")])]})});
            var Q69;
            Q69=makeQuery(id+"F7.opBoolean","COPY",EDGE,{"derivedFrom":makeQuery(id+"F5.opExtrude","SWEPT_EDGE",EDGE,{"disambiguationData":[OSD([sQuery(id+"F4.wireOp",EDGE,"E9.18.1"),sQuery(id+"F4.wireOp",EDGE,"E9.18.3")])]})});
            var Q70;
            Q70=makeQuery(id+"F7.opBoolean","INTERSECT",EDGE,{"derivedFrom":[makeQuery(id+"F5.opExtrude","SWEPT_FACE",FACE,{"disambiguationData":[OSD([sQuery(id+"F4.wireOp",EDGE,"E9.18.3")])]}),makeQuery(id+"F1.opExtrude","SWEPT_FACE",FACE,{"disambiguationData":[OSD([sQuery(id+"F0.wireOp",EDGE,"E0")])]})]});
            var Q71;
            Q71=makeQuery(id+"F7.opBoolean","INTERSECT",EDGE,{"derivedFrom":[makeQuery(id+"F5.opExtrude","SWEPT_FACE",FACE,{"disambiguationData":[OSD([sQuery(id+"F4.wireOp",EDGE,"E9.19.0")])]}),makeQuery(id+"F1.opExtrude","SWEPT_FACE",FACE,{"disambiguationData":[OSD([sQuery(id+"F0.wireOp",EDGE,"E0")])]})]});
            var Q72;
            Q72=makeQuery(id+"F7.opBoolean","COPY",EDGE,{"derivedFrom":makeQuery(id+"F5.opExtrude","SWEPT_EDGE",EDGE,{"disambiguationData":[OSD([sQuery(id+"F4.wireOp",EDGE,"E9.19.0"),sQuery(id+"F4.wireOp",EDGE,"E9.19.1")])]})});
            var Q73;
            Q73=makeQuery(id+"F7.opBoolean","COPY",EDGE,{"derivedFrom":makeQuery(id+"F5.opExtrude","SWEPT_EDGE",EDGE,{"disambiguationData":[OSD([sQuery(id+"F4.wireOp",EDGE,"E9.19.1"),sQuery(id+"F4.wireOp",EDGE,"E9.19.3")])]})});
            var Q74;
            Q74=makeQuery(id+"F7.opBoolean","INTERSECT",EDGE,{"derivedFrom":[makeQuery(id+"F5.opExtrude","SWEPT_FACE",FACE,{"disambiguationData":[OSD([sQuery(id+"F4.wireOp",EDGE,"E9.19.3")])]}),makeQuery(id+"F1.opExtrude","SWEPT_FACE",FACE,{"disambiguationData":[OSD([sQuery(id+"F0.wireOp",EDGE,"E0")])]})]});
            var Q75;
            Q75=makeQuery(id+"F6.opBoolean","INTERSECT",EDGE,{"derivedFrom":[makeQuery(id+"F1.opExtrude","SWEPT_FACE",FACE,{"disambiguationData":[OSD([sQuery(id+"F0.wireOp",EDGE,"E0")])]}),makeQuery(id+"F5.opExtrude","SWEPT_FACE",FACE,{"disambiguationData":[OSD([sQuery(id+"F4.wireOp",EDGE,"E8")])]})]});
            var Q76;
            Q76=makeQuery(id+"F7.opBoolean","COPY",EDGE,{"derivedFrom":makeQuery(id+"F5.opExtrude","SWEPT_EDGE",EDGE,{"disambiguationData":[OSD([sQuery(id+"F4.wireOp",EDGE,"E9.1.1"),sQuery(id+"F4.wireOp",EDGE,"E9.1.3")])]})});
            fillet(context, id + "F8", {"entities" : qUnion([Q0, Q1, Q2, Q3, Q4, Q5, Q6, Q7, Q8, Q9, Q10, Q11, Q12, Q13, Q14, Q15, Q16, Q17, Q18, Q19, Q20, Q21, Q22, Q23, Q24, Q25, Q26, Q27, Q28, Q29, Q30, Q31, Q32, Q33, Q34, Q35, Q36, Q37, Q38, Q39, Q40, Q41, Q42, Q43, Q44, Q45, Q46, Q47, Q48, Q49, Q50, Q51, Q52, Q53, Q54, Q55, Q56, Q57, Q58, Q59, Q60, Q61, Q62, Q63, Q64, Q65, Q66, Q67, Q68, Q69, Q70, Q71, Q72, Q73, Q74, Q75, Q76]), "radius" : 3 * mm, "tangentPropagation" : true, "allowEdgeOverflow" : false});
        }
    });
